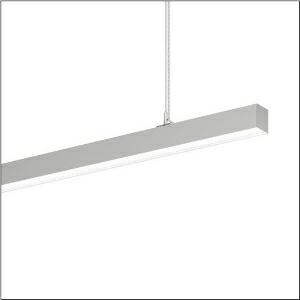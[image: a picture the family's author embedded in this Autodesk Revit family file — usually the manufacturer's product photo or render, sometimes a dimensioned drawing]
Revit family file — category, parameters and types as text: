
# Revit family: silica_r__21_51mx33tbt9s_9dae
name_source: partatom
category: Lighting Fixtures
units: mm (PartAtom-declared; Revit-internal decimal feet)

## family parameters
Cut with Voids When Loaded = No
Host = Face
Light Source = No
Part Type = Normal
Room Calculation Point = No
Round Connector Dimension = Use Diameter
Shared = No

## types (1)
- --- (1 x LED, 7170 lm, 67.4 W, 6500K)
    Apparent Load = 67 VA
    CIE Flux Codes = 78 96 99 56 100
    Color Rendering = 80
    Color Temperature = 6500K
    Default Elevation = 1800 mm
    Description = Silica® 21, office luminaire, primary optical cover: prismatic diffuser, of PMMA, CAT 2 (L<= 3000cd/m²), light emission: direct/indirect distribution, primary light characteristic: symmetric, installation type: suspended mounting, LED, rated luminous flux: 7.170lm, luminous efficacy: 101lm/W, light colour: 8tw, colour temperature: 2700..6500K, control gear: DALI DT8, with terminal, 3+2-pole, max. 2.5mm², mains connection: 220..240V, AC, 50/60Hz, rated input power: 70.8W, luminaire housing, of aluminium, metallic grey (RAL 9006), length: 1.504mm, width: 53mm, height: 53mm, protection rating (complete): IP20, insulation class (complete): insulation class I (protective earthing), certification: CE, permissible operating ambient temperature: 0..+35°C, standard: EN 50419, packaging unit: 1 piece
    Height = 53 mm
    Lamp = 1 x LED
    Lamp Light Flux = 7170 lm
    Lamp Power = 67.4 W
    Lamp count = 1
    Length = 1504 mm
    Luminous efficacy = 106 lm/W
    Manufacturer = Siteco
    ModVariant = No
    Model = 51MX33TBT9S
    Mounting Place = Ceiling
    Mounting Type = Pendant
    Number of Poles = 1
    OnlyDefault = Yes
    Power Factor = 1
    Product Name = Silica® 21
    Product group = office luminaire | ceiling pendant
    ProductGroupID = 903
    Protection Class = Protection class I
    Protection Degree = IP 20
    RLX_Detail_Level = 1
    RLX_Emergency_Light_Flux = 0 lm
    RLX_Emergency_Type = 0
    RLX_Emergency_Type_DB = No
    RlxData = <blob elided: 20185 chars, md5=5ba4d5c8>
    Socket = socket
    Standby Power = 0 W
    System Light Flux = 7170 lm
    System Power = 67 W
    Type Comments = individual setting
    Type Image = l_1335864.jpg
    URL = http://relux.com
    VarID = @adj_161219
    Voltage = 0 V
    Weight = 0.00 kg
    Width = 53 mm

## geometry (parser evidence)
native form markers: Blend x4, Sweep x12
no freeform markers — native parametric forms only
